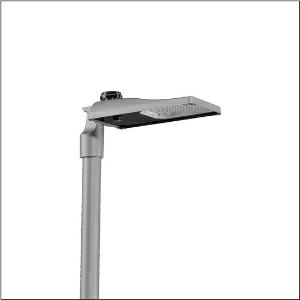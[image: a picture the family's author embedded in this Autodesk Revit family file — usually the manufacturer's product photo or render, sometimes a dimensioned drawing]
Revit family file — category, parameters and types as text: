
# Revit family: streetlight_sl_31_mini___st1_0a_5xh2d3bm08ja_c740
name_source: partatom
category: Lighting Fixtures
units: mm (PartAtom-declared; Revit-internal decimal feet)

## family parameters
Cut with Voids When Loaded = No
Host = Face
Light Source = No
Part Type = Normal
Room Calculation Point = No
Round Connector Dimension = Use Diameter
Shared = No

## types (1)
- --- (1 x LED, 12270 lm, 82.5 W, 3000K)
    Apparent Load = 83 VA
    CIE Flux Codes = 40 73 97 100 100
    Color Rendering = 70
    Color Temperature = 3000K
    Default Elevation = 1800 mm
    Description = Streetlight SL 31 mini, mast luminaire, primary light control with lens, of PMMA, primary optical cover: cover, of toughened safety glass, transparent, light distribution: ST1.0a, light emission: direct distribution, primary light characteristic: asymmetric, installation type: post-top, side-entry, LED, High Power LED, rated luminous flux: 12.270lm, luminous efficacy: 149lm/W, light colour: 730, colour temperature: 3000K, control: presetting dimming linear, flexible luminous flux parameterisation, time-dependent luminous flux control, constant luminous flux control, intelligent temperature release in ECG and LED module, overheat protection, with cable H07RN-F 3x 1.5mm², mains connection: 220..240V, AC, 50/60Hz, connection cable pre-assembled, cable length: 10,5m, start of lifetime: 83W, end of service life: 90W, reduction: 37W, luminaire housing, of diecast aluminium, powder-coated, Siteco® metallic grey (DB 702S), corrosivity category C5 high according to DIN EN ISO 12944, no sealing on luminaire upper side, inclination: -15°..+20° (post-top) | -20°..+20° (side-entry), adjustable in 5° steps, mast flange (76/60mm) included as standard, multi-level sealing system, sealing non-destructively replaceable, Smart Interface below, protection rating (complete): IP66, insulation class (complete): insulation class I (protective earthing), certification: CE, ENEC, ENEC+, VDE, UKCA, impact resistance: IK09, permissible operating ambient temperature for outdoor applications: -40..+50°C, standard-compliant lighting for roads and squares, packaging unit: 1 piece

Light Distribution: ST1.0a
    Height = 76 mm
    Lamp = 1 x LED
    Lamp Light Flux = 12270 lm
    Lamp Power = 82.5 W
    Lamp count = 1
    Length = 547 mm
    Luminous efficacy = 149 lm/W
    Manufacturer = Siteco
    ModVariant = No
    Model = 5XH2D3BM08JA
    Number of Poles = 1
    OnlyDefault = Yes
    Power Factor = 1
    Product Name = Streetlight SL 31 mini | ST1.0a
    Product group = mast luminaire | pylon top
    ProductGroupID = 6100
    Protection Class = Protection class I
    Protection Degree = IP 66
    RLX_Detail_Level = 1
    RLX_Emergency_Light_Flux = 0 lm
    RLX_Emergency_Type = 0
    RLX_Emergency_Type_DB = No
    RlxData = <blob elided: 40625 chars, md5=09d3edde>
    Socket = socket
    Standby Power = 0 W
    System Light Flux = 12270 lm
    System Power = 83 W
    Type Comments = factory setting: luminous flux: 100 % | dim-lin: 254 | 870 mA
    Type Image = l_1300324.jpg
    URL = http://relux.com
    VarID = @adj_008175
    Voltage = 0 V
    Weight = 0.00 kg
    Width = 265 mm

## geometry (parser evidence)
native form markers: Blend x4, Sweep x9
no freeform markers — native parametric forms only
